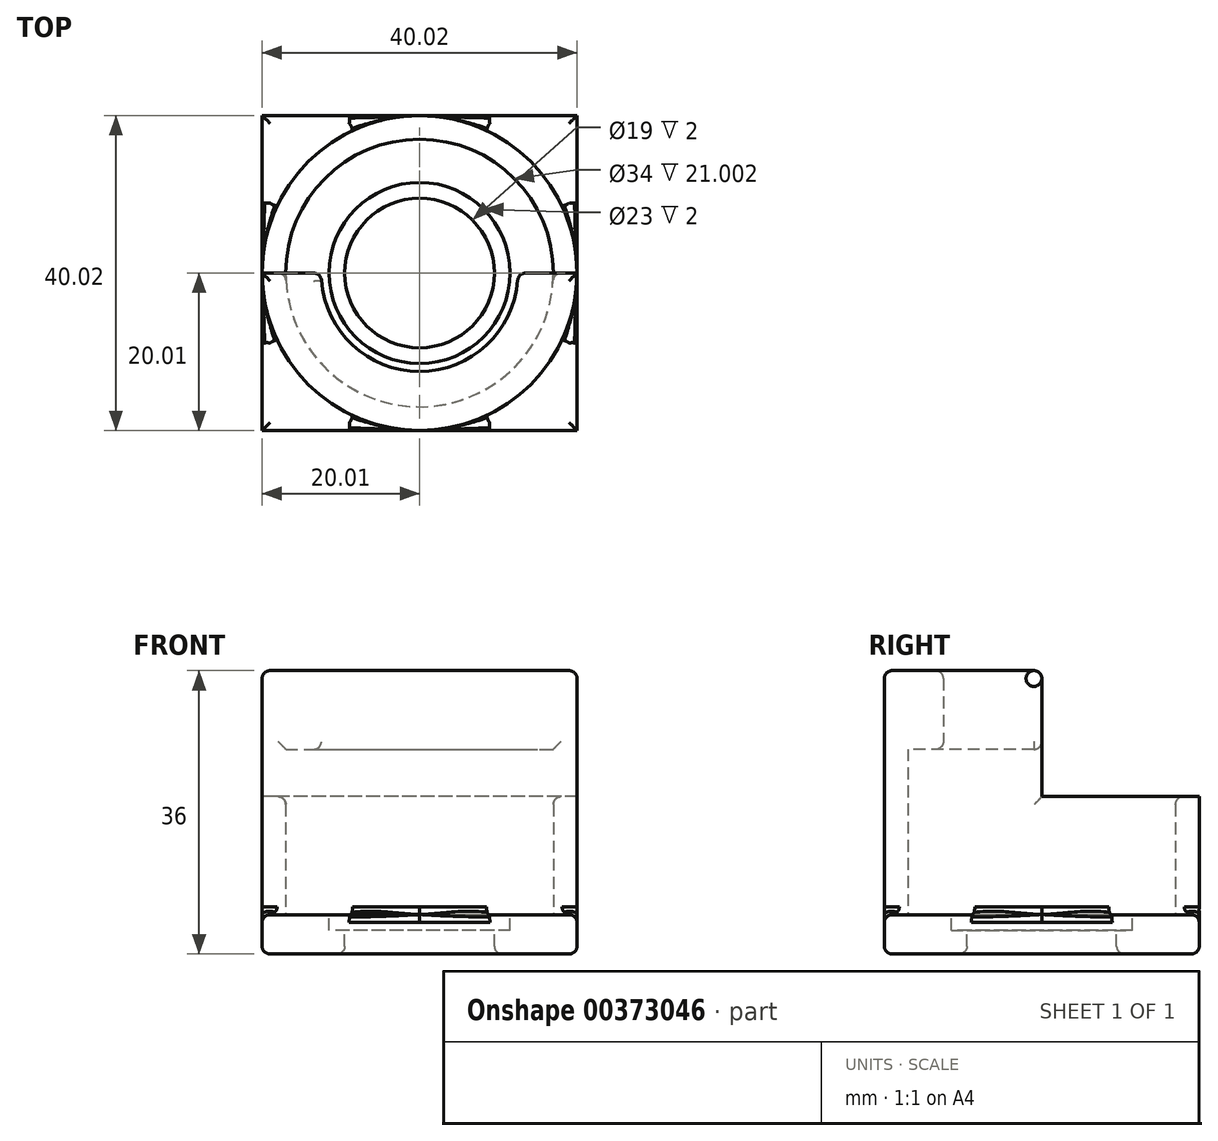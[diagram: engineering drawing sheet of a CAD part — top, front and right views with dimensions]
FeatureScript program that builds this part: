
annotation { "Feature Type Name" : "Feature", "Feature Type Description" : "" }
export const myFeature = defineFeature(function(context is Context, id is Id, definition is map)
    precondition{}
    {
        {
            var Q0;
            Q0=qCreatedBy(makeId("Top.planeOp"),FACE);
            var sketch = newSketch(context, id + "F0", { "sketchPlane" : qUnion([Q0])});
            skLineSegment(sketch, "E0.bottom", {"start": v(20, 20) * mm, "end": v(-20, 20) * mm});
            skLineSegment(sketch, "E0.top", {"start": v(20, -20) * mm, "end": v(-20, -20) * mm});
            skLineSegment(sketch, "E0.left", {"start": v(20, 20) * mm, "end": v(20, -20) * mm});
            skLineSegment(sketch, "E0.right", {"start": v(-20, 20) * mm, "end": v(-20, -20) * mm});
            skPoint(sketch, "E0.middle", {"position": v(0, 0) * mm});
            skSolve(sketch);
        }
        {
            var Q0;
            Q0 = qSketchRegion(id + "F0", true);
            extrude(context, id + "F1", {"entities" : qUnion([Q0]), "depth" : 5 * mm});
        }
        {
            var Q0;
            Q0=makeQuery(id+"F1.opExtrude","CAP_FACE",FACE,{"disambiguationData":[OSD([sQuery(id+"F0.wireOp",EDGE,"E0.bottom"),sQuery(id+"F0.wireOp",EDGE,"E0.top"),sQuery(id+"F0.wireOp",EDGE,"E0.left"),sQuery(id+"F0.wireOp",EDGE,"E0.right")])],"isStart":false});
            var sketch = newSketch(context, id + "F2", { "sketchPlane" : qUnion([Q0])});
            skCircle(sketch, "E1", {"center": v(0, 0) * mm, "radius": 9.5 * mm});
            skSolve(sketch);
        }
        {
            var Q0;
            Q0 = qSketchRegion(id + "F2", true);
            extrude(context, id + "F3", {"entities" : qUnion([Q0]), "operationType" : NewBodyOperationType.REMOVE, "endBound" : BoundingType.THROUGH_ALL, "oppositeDirection" : true, "depth" : 25 * mm});
        }
        {
            var Q0;
            Q0=makeQuery(id+"F1.opExtrude","CAP_FACE",FACE,{"disambiguationData":[OSD([sQuery(id+"F0.wireOp",EDGE,"E0.bottom"),sQuery(id+"F0.wireOp",EDGE,"E0.top"),sQuery(id+"F0.wireOp",EDGE,"E0.left"),sQuery(id+"F0.wireOp",EDGE,"E0.right")])],"isStart":false});
            var sketch = newSketch(context, id + "F4", { "sketchPlane" : qUnion([Q0])});
            skCircle(sketch, "E2", {"center": v(0, 0) * mm, "radius": 17 * mm});
            skCircle(sketch, "E3", {"center": v(0, 0) * mm, "radius": 20 * mm});
            skSolve(sketch);
        }
        {
            var Q0;
            Q0 = qSketchRegion(id + "F4", true);
            extrude(context, id + "F5", {"entities" : qUnion([Q0]), "operationType" : NewBodyOperationType.ADD, "depth" : 14 * mm});
        }
        {
            var Q0;
            Q0=makeQuery(id+"F5.opExtrude","CAP_FACE",FACE,{"disambiguationData":[OSD([sQuery(id+"F4.wireOp",EDGE,"E2"),sQuery(id+"F4.wireOp",EDGE,"E3")])],"isStart":false});
            var sketch = newSketch(context, id + "F6", { "sketchPlane" : qUnion([Q0])});
            skCircle(sketch, "E4", {"center": v(0, 0) * mm, "radius": 17 * mm});
            skCircle(sketch, "E5", {"center": v(0, 0) * mm, "radius": 20 * mm});
            skSolve(sketch);
        }
        {
            var Q0;
            Q0 = qSketchRegion(id + "F6", true);
            extrude(context, id + "F7", {"entities" : qUnion([Q0]), "operationType" : NewBodyOperationType.ADD, "depth" : 7 * mm});
        }
        {
            var Q0;
            Q0=makeQuery(id+"F7.opExtrude","CAP_FACE",FACE,{"disambiguationData":[OSD([sQuery(id+"F6.wireOp",EDGE,"E4"),sQuery(id+"F6.wireOp",EDGE,"E5")])],"isStart":false});
            var sketch = newSketch(context, id + "F8", { "sketchPlane" : qUnion([Q0])});
            skCircle(sketch, "E6", {"center": v(0, 0) * mm, "radius": 12.5 * mm});
            skCircle(sketch, "E7", {"center": v(0, 0) * mm, "radius": 20 * mm});
            skSolve(sketch);
        }
        {
            var Q0;
            Q0 = qSketchRegion(id + "F8", true);
            extrude(context, id + "F9", {"entities" : qUnion([Q0]), "operationType" : NewBodyOperationType.ADD, "depth" : 10 * mm});
        }
        {
            var Q0;
            Q0=qCreatedBy(makeId("Front.planeOp"),FACE);
            var sketch = newSketch(context, id + "F10", { "sketchPlane" : qUnion([Q0])});
            skLineSegment(sketch, "E8.bottom", {"start": v(154.58, 261.38) * mm, "end": v(-153.4, 261.38) * mm});
            skLineSegment(sketch, "E8.top", {"start": v(154.58, 20) * mm, "end": v(-153.4, 20) * mm});
            skLineSegment(sketch, "E8.left", {"start": v(154.58, 261.38) * mm, "end": v(154.58, 20) * mm});
            skLineSegment(sketch, "E8.right", {"start": v(-153.4, 261.38) * mm, "end": v(-153.4, 20) * mm});
            skSolve(sketch);
        }
        {
            var Q0;
            Q0 = qSketchRegion(id + "F10", true);
            extrude(context, id + "F11", {"entities" : qUnion([Q0]), "operationType" : NewBodyOperationType.REMOVE, "oppositeDirection" : true, "depth" : 25 * mm});
        }
        {
            var Q0;
            Q0=makeQuery(id+"F9.opExtrude","CAP_EDGE",EDGE,{"disambiguationData":[OSD([sQuery(id+"F8.wireOp",EDGE,"E6")])],"isStart":true});
            var Q1;
            {var subQ0=sQuery(id+"F0.wireOp",EDGE,"E0.bottom");var subQ1=sQuery(id+"F0.wireOp",EDGE,"E0.left");var subQ2=makeQuery(id+"F1.opExtrude","CAP_FACE",FACE,{"disambiguationData":[OSD([subQ0,sQuery(id+"F0.wireOp",EDGE,"E0.top"),subQ1,sQuery(id+"F0.wireOp",EDGE,"E0.right")])],"isStart":false});Q1=makeQuery(id+"F5.boolean.opBoolean","SPLIT",FACE,{"disambiguationData":[TD([makeQuery(id+"F1.opExtrude","SWEPT_FACE",FACE,{"disambiguationData":[OSD([subQ0])]}),subQ2,makeQuery(id+"F1.opExtrude","SWEPT_FACE",FACE,{"disambiguationData":[OSD([subQ1])]}),makeQuery(id+"F5.opExtrude","SWEPT_FACE",FACE,{"disambiguationData":[OSD([sQuery(id+"F4.wireOp",EDGE,"E3")])]})])],"derivedFrom":subQ2});}
            var Q2;
            {var subQ0=sQuery(id+"F0.wireOp",EDGE,"E0.bottom");var subQ1=sQuery(id+"F0.wireOp",EDGE,"E0.right");var subQ2=makeQuery(id+"F1.opExtrude","CAP_FACE",FACE,{"disambiguationData":[OSD([subQ0,sQuery(id+"F0.wireOp",EDGE,"E0.top"),sQuery(id+"F0.wireOp",EDGE,"E0.left"),subQ1])],"isStart":false});Q2=makeQuery(id+"F5.boolean.opBoolean","SPLIT",FACE,{"disambiguationData":[TD([makeQuery(id+"F1.opExtrude","SWEPT_FACE",FACE,{"disambiguationData":[OSD([subQ0])]}),subQ2,makeQuery(id+"F1.opExtrude","SWEPT_FACE",FACE,{"disambiguationData":[OSD([subQ1])]}),makeQuery(id+"F5.opExtrude","SWEPT_FACE",FACE,{"disambiguationData":[OSD([sQuery(id+"F4.wireOp",EDGE,"E3")])]})])],"derivedFrom":subQ2});}
            var Q3;
            {var subQ0=sQuery(id+"F0.wireOp",EDGE,"E0.left");var subQ1=sQuery(id+"F0.wireOp",EDGE,"E0.top");Q3=makeQuery(id+"F5.boolean.opBoolean","SPLIT",EDGE,{"disambiguationData":[TD([makeQuery(id+"F1.opExtrude","SWEPT_FACE",FACE,{"disambiguationData":[OSD([subQ0])]})])],"derivedFrom":makeQuery(id+"F1.opExtrude","CAP_EDGE",EDGE,{"disambiguationData":[OSD([subQ1])],"isStart":false})});}
            var Q4;
            {var subQ0=sQuery(id+"F0.wireOp",EDGE,"E0.left");var subQ1=sQuery(id+"F0.wireOp",EDGE,"E0.top");var subQ2=makeQuery(id+"F1.opExtrude","CAP_FACE",FACE,{"disambiguationData":[OSD([sQuery(id+"F0.wireOp",EDGE,"E0.bottom"),subQ1,subQ0,sQuery(id+"F0.wireOp",EDGE,"E0.right")])],"isStart":false});Q4=makeQuery(id+"F5.boolean.opBoolean","SPLIT",FACE,{"disambiguationData":[TD([subQ2,makeQuery(id+"F1.opExtrude","SWEPT_FACE",FACE,{"disambiguationData":[OSD([subQ1])]}),makeQuery(id+"F1.opExtrude","SWEPT_FACE",FACE,{"disambiguationData":[OSD([subQ0])]}),makeQuery(id+"F5.opExtrude","SWEPT_FACE",FACE,{"disambiguationData":[OSD([sQuery(id+"F4.wireOp",EDGE,"E3")])]})])],"derivedFrom":subQ2});}
            var Q5;
            {var subQ0=sQuery(id+"F0.wireOp",EDGE,"E0.right");var subQ1=sQuery(id+"F0.wireOp",EDGE,"E0.top");var subQ2=makeQuery(id+"F1.opExtrude","CAP_FACE",FACE,{"disambiguationData":[OSD([sQuery(id+"F0.wireOp",EDGE,"E0.bottom"),subQ1,sQuery(id+"F0.wireOp",EDGE,"E0.left"),subQ0])],"isStart":false});Q5=makeQuery(id+"F5.boolean.opBoolean","SPLIT",FACE,{"disambiguationData":[TD([subQ2,makeQuery(id+"F1.opExtrude","SWEPT_FACE",FACE,{"disambiguationData":[OSD([subQ1])]}),makeQuery(id+"F1.opExtrude","SWEPT_FACE",FACE,{"disambiguationData":[OSD([subQ0])]}),makeQuery(id+"F5.opExtrude","SWEPT_FACE",FACE,{"disambiguationData":[OSD([sQuery(id+"F4.wireOp",EDGE,"E3")])]})])],"derivedFrom":subQ2});}
            var Q6;
            Q6=makeQuery(id+"F1.opExtrude","CAP_FACE",FACE,{"disambiguationData":[OSD([sQuery(id+"F0.wireOp",EDGE,"E0.bottom"),sQuery(id+"F0.wireOp",EDGE,"E0.top"),sQuery(id+"F0.wireOp",EDGE,"E0.left"),sQuery(id+"F0.wireOp",EDGE,"E0.right")])],"isStart":true});
            var Q7;
            Q7=makeQuery(id+"F9ri2nNTRFE8rnC_1.opExtrude","CAP_FACE",FACE,{"disambiguationData":[OSD([sQuery(id+"F170pczUVJpTuFL_1.wireOp",EDGE,"Cqm2Cm66-7COH-fpxb-ojco-9J8XW2wMW0oD")])],"isStart":false});
            var Q8;
            Q8=makeQuery(id+"F5.opExtrude","CAP_EDGE",EDGE,{"disambiguationData":[OSD([sQuery(id+"F4.wireOp",EDGE,"E2")])],"isStart":false});
            fillet(context, id + "F12", {"entities" : qUnion([Q0, Q1, Q2, Q3, Q4, Q5, Q6, Q7, Q8]), "radius" : 1 * mm, "tangentPropagation" : true, "allowEdgeOverflow" : false});
        }
        {
            var Q0;
            Q0=makeQuery(id+"F5.boolean.opBoolean","SPLIT",FACE,{"disambiguationData":[TD([makeQuery(id+"F3.boolean.opBoolean","COPY",FACE,{"derivedFrom":makeQuery(id+"F3.opExtrude","SWEPT_FACE",FACE,{"disambiguationData":[OSD([sQuery(id+"F2.wireOp",EDGE,"E1")])]})}),makeQuery(id+"F5.opExtrude","SWEPT_FACE",FACE,{"disambiguationData":[OSD([sQuery(id+"F4.wireOp",EDGE,"E2")])]})])],"derivedFrom":makeQuery(id+"F1.opExtrude","CAP_FACE",FACE,{"disambiguationData":[OSD([sQuery(id+"F0.wireOp",EDGE,"E0.bottom"),sQuery(id+"F0.wireOp",EDGE,"E0.top"),sQuery(id+"F0.wireOp",EDGE,"E0.left"),sQuery(id+"F0.wireOp",EDGE,"E0.right")])],"isStart":false})});
            var sketch = newSketch(context, id + "F13", { "sketchPlane" : qUnion([Q0])});
            skCircle(sketch, "E9", {"center": v(0, 0) * mm, "radius": 11.5 * mm});
            skSolve(sketch);
        }
        {
            var Q0;
            Q0=makeQuery(id+"F13.imprint","IMPRINT",FACE,{"disambiguationData":[TD([[makeQuery(id+"F13.imprint","IMPRINT",EDGE,{"derivedFrom":sQuery(id+"F13.wireOp",EDGE,"E9")}),1.0]])]});
            extrude(context, id + "F14", {"entities" : qUnion([Q0]), "operationType" : NewBodyOperationType.REMOVE, "oppositeDirection" : true, "depth" : 2 * mm});
        }
        {
            var Q0;
            Q0=makeQuery(id+"F14.boolean.opBoolean","COPY",EDGE,{"derivedFrom":makeQuery(id+"F14.opExtrude","CAP_EDGE",EDGE,{"disambiguationData":[OSD([sQuery(id+"F13.wireOp",EDGE,"E9")])],"isStart":true})});
            var Q1;
            Q1=makeQuery(id+"F11.boolean.opBoolean","INTERSECT",EDGE,{"derivedFrom":[makeQuery(id+"F7.boolean.opBoolean","MERGE",FACE,{"derivedFrom":[makeQuery(id+"F5.opExtrude","SWEPT_FACE",FACE,{"disambiguationData":[OSD([sQuery(id+"F4.wireOp",EDGE,"E2")])]}),makeQuery(id+"F7.opExtrude","SWEPT_FACE",FACE,{"disambiguationData":[OSD([sQuery(id+"F6.wireOp",EDGE,"E4")])]})]}),makeQuery(id+"F11.opExtrude","SWEPT_FACE",FACE,{"disambiguationData":[OSD([sQuery(id+"F10.wireOp",EDGE,"E8.top")])]})]});
            var Q2;
            Q2=makeQuery(id+"F9.opExtrude","CAP_FACE",FACE,{"disambiguationData":[OSD([sQuery(id+"F8.wireOp",EDGE,"E6"),sQuery(id+"F8.wireOp",EDGE,"E7")])],"isStart":false});
            var Q3;
            Q3=makeQuery(id+"F11.boolean.opBoolean","INTERSECT",EDGE,{"disambiguationData":[OD(1.0)],"derivedFrom":[makeQuery(id+"F7.boolean.opBoolean","MERGE",FACE,{"derivedFrom":[makeQuery(id+"F5.opExtrude","SWEPT_FACE",FACE,{"disambiguationData":[OSD([sQuery(id+"F4.wireOp",EDGE,"E2")])]}),makeQuery(id+"F7.opExtrude","SWEPT_FACE",FACE,{"disambiguationData":[OSD([sQuery(id+"F6.wireOp",EDGE,"E4")])]})]}),makeQuery(id+"F11.opExtrude","CAP_FACE",FACE,{"disambiguationData":[OSD([sQuery(id+"F10.wireOp",EDGE,"E8.bottom"),sQuery(id+"F10.wireOp",EDGE,"E8.top"),sQuery(id+"F10.wireOp",EDGE,"E8.left"),sQuery(id+"F10.wireOp",EDGE,"E8.right")])],"isStart":true})]});
            var Q4;
            Q4=makeQuery(id+"F11.boolean.opBoolean","INTERSECT",EDGE,{"disambiguationData":[OD(0.0)],"derivedFrom":[makeQuery(id+"F7.boolean.opBoolean","MERGE",FACE,{"derivedFrom":[makeQuery(id+"F5.opExtrude","SWEPT_FACE",FACE,{"disambiguationData":[OSD([sQuery(id+"F4.wireOp",EDGE,"E2")])]}),makeQuery(id+"F7.opExtrude","SWEPT_FACE",FACE,{"disambiguationData":[OSD([sQuery(id+"F6.wireOp",EDGE,"E4")])]})]}),makeQuery(id+"F11.opExtrude","CAP_FACE",FACE,{"disambiguationData":[OSD([sQuery(id+"F10.wireOp",EDGE,"E8.bottom"),sQuery(id+"F10.wireOp",EDGE,"E8.top"),sQuery(id+"F10.wireOp",EDGE,"E8.left"),sQuery(id+"F10.wireOp",EDGE,"E8.right")])],"isStart":true})]});
            var Q5;
            Q5=makeQuery(id+"F11.boolean.opBoolean","INTERSECT",EDGE,{"disambiguationData":[OD(1.0)],"derivedFrom":[makeQuery(id+"F9.opExtrude","CAP_FACE",FACE,{"disambiguationData":[OSD([sQuery(id+"F8.wireOp",EDGE,"E6"),sQuery(id+"F8.wireOp",EDGE,"E7")])],"isStart":true}),makeQuery(id+"F11.opExtrude","CAP_FACE",FACE,{"disambiguationData":[OSD([sQuery(id+"F10.wireOp",EDGE,"E8.bottom"),sQuery(id+"F10.wireOp",EDGE,"E8.top"),sQuery(id+"F10.wireOp",EDGE,"E8.left"),sQuery(id+"F10.wireOp",EDGE,"E8.right")])],"isStart":true})]});
            var Q6;
            Q6=makeQuery(id+"F11.boolean.opBoolean","INTERSECT",EDGE,{"disambiguationData":[OD(0.0)],"derivedFrom":[makeQuery(id+"F9.opExtrude","CAP_FACE",FACE,{"disambiguationData":[OSD([sQuery(id+"F8.wireOp",EDGE,"E6"),sQuery(id+"F8.wireOp",EDGE,"E7")])],"isStart":true}),makeQuery(id+"F11.opExtrude","CAP_FACE",FACE,{"disambiguationData":[OSD([sQuery(id+"F10.wireOp",EDGE,"E8.bottom"),sQuery(id+"F10.wireOp",EDGE,"E8.top"),sQuery(id+"F10.wireOp",EDGE,"E8.left"),sQuery(id+"F10.wireOp",EDGE,"E8.right")])],"isStart":true})]});
            fillet(context, id + "F15", {"entities" : qUnion([Q0, Q1, Q2, Q3, Q4, Q5, Q6]), "radius" : 1 * mm, "tangentPropagation" : true, "allowEdgeOverflow" : false});
        }
    });
